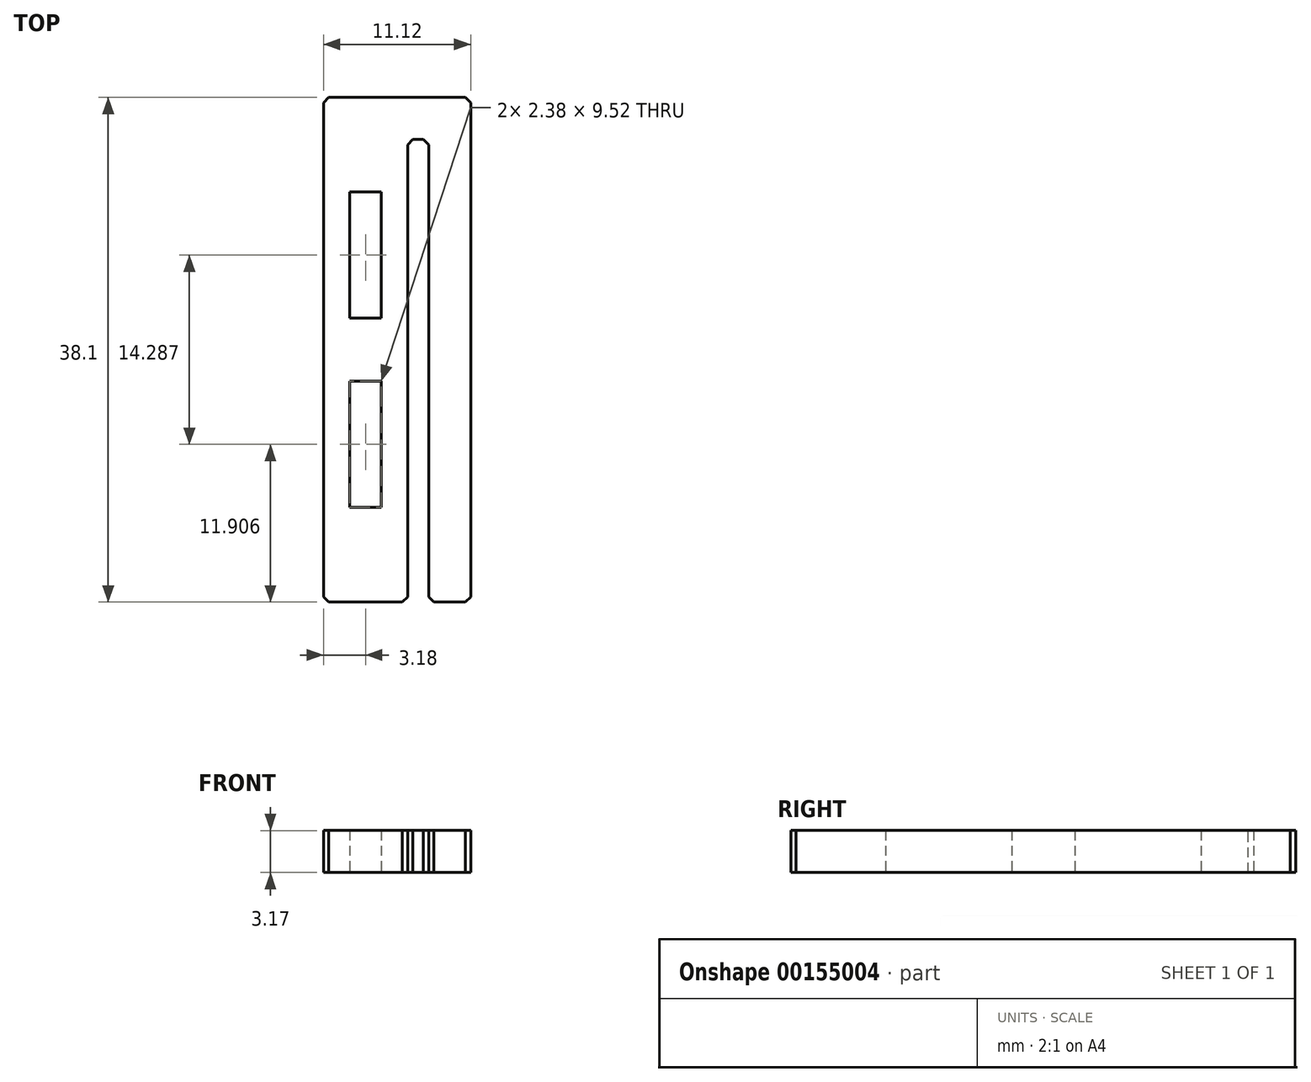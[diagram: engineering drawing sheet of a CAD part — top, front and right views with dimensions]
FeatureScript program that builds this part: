
annotation { "Feature Type Name" : "Feature", "Feature Type Description" : "" }
export const myFeature = defineFeature(function(context is Context, id is Id, definition is map)
    precondition{}
    {
        {
            var Q0;
            Q0=qCreatedBy(makeId("Top.planeOp"),FACE);
            var sketch = newSketch(context, id + "F0", { "sketchPlane" : qUnion([Q0])});
            skLineSegment(sketch, "E0.bottom", {"start": v(3.18, 19.05) * mm, "end": v(-3.18, 19.05) * mm});
            skLineSegment(sketch, "E0.top", {"start": v(3.18, -19.05) * mm, "end": v(-3.18, -19.05) * mm});
            skLineSegment(sketch, "E0.left", {"start": v(3.18, 19.05) * mm, "end": v(3.18, -19.05) * mm});
            skLineSegment(sketch, "E0.right", {"start": v(-3.18, 19.05) * mm, "end": v(-3.18, -19.05) * mm});
            skPoint(sketch, "E0.middle", {"position": v(0, 0) * mm});
            skLineSegment(sketch, "E1", {"start": v(-3.17, 0) * mm, "end": v(3.18, 0) * mm, "construction": true});
            skLineSegment(sketch, "E2", {"start": v(0, 0) * mm, "end": v(0, 19.05) * mm, "construction": true});
            skLineSegment(sketch, "E3.bottom", {"start": v(-1.2, 2.38) * mm, "end": v(1.2, 2.38) * mm});
            skLineSegment(sketch, "E3.top", {"start": v(-1.2, 11.9) * mm, "end": v(1.2, 11.9) * mm});
            skLineSegment(sketch, "E3.left", {"start": v(-1.2, 2.38) * mm, "end": v(-1.2, 11.9) * mm});
            skLineSegment(sketch, "E3.right", {"start": v(1.2, 2.38) * mm, "end": v(1.2, 11.9) * mm});
            skPoint(sketch, "E3.middle", {"position": v(0, 9.53) * mm});
            skLineSegment(sketch, "E4.MirrorCS", {"start": v(-1.2, -2.38) * mm, "end": v(-1.2, -11.9) * mm});
            skLineSegment(sketch, "E5.MirrorCS", {"start": v(-1.2, -2.38) * mm, "end": v(1.2, -2.38) * mm});
            skLineSegment(sketch, "E6.MirrorCS", {"start": v(1.2, -2.38) * mm, "end": v(1.2, -11.9) * mm});
            skLineSegment(sketch, "E7.MirrorCS", {"start": v(-1.2, -11.9) * mm, "end": v(1.2, -11.9) * mm});
            skLineSegment(sketch, "E8", {"start": v(3.18, 19.05) * mm, "end": v(7.94, 19.05) * mm});
            skLineSegment(sketch, "E9", {"start": v(7.94, 19.05) * mm, "end": v(7.94, -19.05) * mm});
            skLineSegment(sketch, "E10.0", {"start": v(4.76, 15.88) * mm, "end": v(4.76, -19.05) * mm});
            skLineSegment(sketch, "E10.1", {"start": v(3.18, 15.88) * mm, "end": v(4.76, 15.88) * mm});
            skLineSegment(sketch, "E11", {"start": v(7.94, -19.05) * mm, "end": v(4.76, -19.05) * mm});
            skSolve(sketch);
        }
        {
            var Q0;
            Q0 = qSketchRegion(id + "F0", true);
            extrude(context, id + "F1", {"entities" : qUnion([Q0]), "depth" : 3.17 * mm});
        }
        {
            var Q0;
            Q0=makeQuery(id+"F1.opExtrude","SWEPT_EDGE",EDGE,{"disambiguationData":[OSD([sQuery(id+"F0.wireOp",EDGE,"E10.0"),sQuery(id+"F0.wireOp",EDGE,"E10.1")])]});
            var Q1;
            Q1=makeQuery(id+"F1.opExtrude","SWEPT_EDGE",EDGE,{"disambiguationData":[OSD([sQuery(id+"F0.wireOp",EDGE,"E0.left"),sQuery(id+"F0.wireOp",EDGE,"E10.1")])]});
            var Q2;
            Q2=makeQuery(id+"F1.opExtrude","SWEPT_EDGE",EDGE,{"disambiguationData":[OSD([sQuery(id+"F0.wireOp",EDGE,"E8"),sQuery(id+"F0.wireOp",EDGE,"E9")])]});
            var Q3;
            Q3=makeQuery(id+"F1.opExtrude","SWEPT_EDGE",EDGE,{"disambiguationData":[OSD([sQuery(id+"F0.wireOp",EDGE,"E0.bottom"),sQuery(id+"F0.wireOp",EDGE,"E0.right")])]});
            var Q4;
            Q4=makeQuery(id+"F1.opExtrude","SWEPT_EDGE",EDGE,{"disambiguationData":[OSD([sQuery(id+"F0.wireOp",EDGE,"E9"),sQuery(id+"F0.wireOp",EDGE,"E11")])]});
            var Q5;
            Q5=makeQuery(id+"F1.opExtrude","SWEPT_EDGE",EDGE,{"disambiguationData":[OSD([sQuery(id+"F0.wireOp",EDGE,"E10.0"),sQuery(id+"F0.wireOp",EDGE,"E11")])]});
            var Q6;
            Q6=makeQuery(id+"F1.opExtrude","SWEPT_EDGE",EDGE,{"disambiguationData":[OSD([sQuery(id+"F0.wireOp",EDGE,"E0.top"),sQuery(id+"F0.wireOp",EDGE,"E0.left")])]});
            var Q7;
            Q7=makeQuery(id+"F1.opExtrude","SWEPT_EDGE",EDGE,{"disambiguationData":[OSD([sQuery(id+"F0.wireOp",EDGE,"E0.top"),sQuery(id+"F0.wireOp",EDGE,"E0.right")])]});
            chamfer(context, id + "F2", {"entities" : qUnion([Q0, Q1, Q2, Q3, Q4, Q5, Q6, Q7]), "width" : 0.4 * mm, "tangentPropagation" : true});
        }
    });
